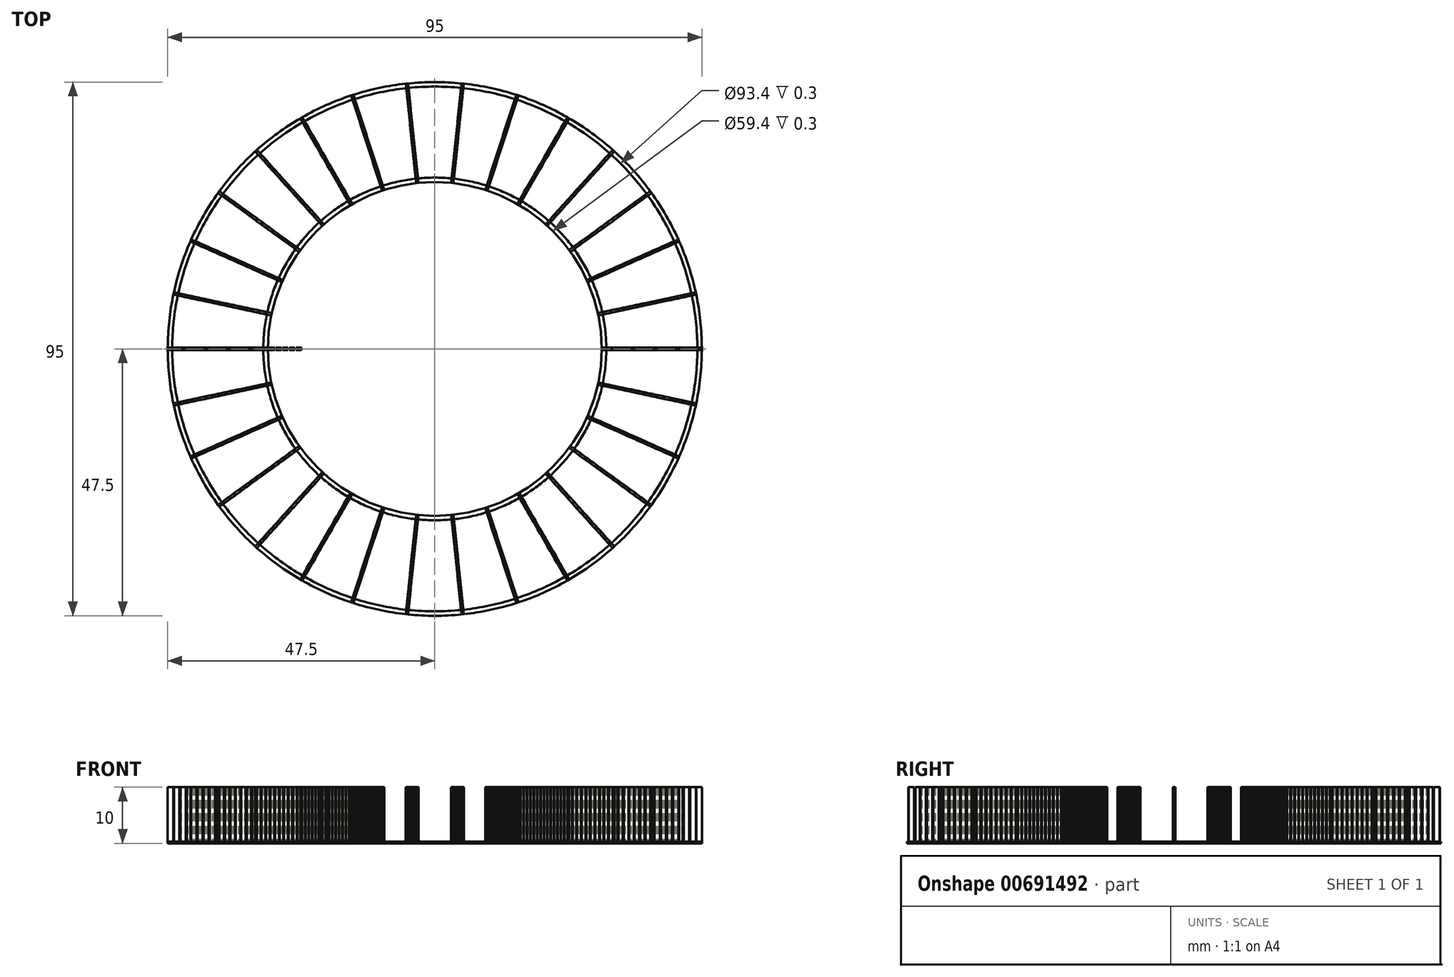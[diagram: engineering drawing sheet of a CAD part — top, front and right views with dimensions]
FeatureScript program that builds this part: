
annotation { "Feature Type Name" : "Feature", "Feature Type Description" : "" }
export const myFeature = defineFeature(function(context is Context, id is Id, definition is map)
    precondition{}
    {
        {
            var Q0;
            Q0=qCreatedBy(makeId("Top.planeOp"),FACE);
            var sketch = newSketch(context, id + "F0", { "sketchPlane" : qUnion([Q0])});
            skCircle(sketch, "E0", {"center": v(0, 0) * mm, "radius": 47.5 * mm, "construction": true});
            skCircle(sketch, "E1", {"center": v(0, 0) * mm, "radius": 30 * mm, "construction": true});
            skLineSegment(sketch, "E2", {"start": v(-30, 0) * mm, "end": v(-47.5, 0) * mm, "construction": true});
            skLineSegment(sketch, "E3.bottom", {"start": v(-30, 0.2) * mm, "end": v(-47.5, 0.2) * mm});
            skLineSegment(sketch, "E3.top", {"start": v(-30, -0.21) * mm, "end": v(-47.5, -0.21) * mm});
            skLineSegment(sketch, "E3.left", {"start": v(-30, 0.2) * mm, "end": v(-30, -0.2) * mm});
            skLineSegment(sketch, "E3.right", {"start": v(-47.5, 0.21) * mm, "end": v(-47.5, -0.21) * mm});
            skSolve(sketch);
        }
        {
            var Q0;
            Q0=makeQuery(id+"F0.imprint","IMPRINT",FACE,{"disambiguationData":[TD([[makeQuery(id+"F0.imprint","IMPRINT",EDGE,{"derivedFrom":sQuery(id+"F0.wireOp",EDGE,"E3.bottom")}),1.0]])]});
            extrude(context, id + "F1", {"entities" : qUnion([Q0]), "depth" : 0.3 * mm, "offsetDistance" : 25 * mm});
        }
        {
            var Q0;
            Q0=qCreatedBy(makeId("Top.planeOp"),FACE);
            var sketch = newSketch(context, id + "F2", { "sketchPlane" : qUnion([Q0])});
            skCircle(sketch, "E4", {"center": v(0, 0) * mm, "radius": 47.5 * mm, "construction": true});
            skCircle(sketch, "E5", {"center": v(0, 0) * mm, "radius": 35 * mm, "construction": true});
            skLineSegment(sketch, "E6", {"start": v(-35, 0) * mm, "end": v(-47.5, 0) * mm, "construction": true});
            skLineSegment(sketch, "E7.bottom", {"start": v(-47.5, 0.2) * mm, "end": v(-46.5, 0.2) * mm});
            skLineSegment(sketch, "E7.top", {"start": v(-47.5, -0.21) * mm, "end": v(-46.5, -0.21) * mm});
            skLineSegment(sketch, "E7.left", {"start": v(-47.5, 0.21) * mm, "end": v(-47.5, -0.21) * mm});
            skLineSegment(sketch, "E7.right", {"start": v(-46.5, 0.21) * mm, "end": v(-46.5, -0.21) * mm});
            skLineSegment(sketch, "E8.1.0.0", {"start": v(-46.3, 0.2) * mm, "end": v(-45.3, 0.2) * mm});
            skLineSegment(sketch, "E8.1.0.1", {"start": v(-45.3, 0.21) * mm, "end": v(-45.3, -0.21) * mm});
            skLineSegment(sketch, "E8.1.0.2", {"start": v(-46.3, -0.21) * mm, "end": v(-45.3, -0.21) * mm});
            skLineSegment(sketch, "E8.1.0.3", {"start": v(-46.3, 0.21) * mm, "end": v(-46.3, -0.21) * mm});
            skLineSegment(sketch, "E8.2.0.0", {"start": v(-45.1, 0.2) * mm, "end": v(-44.1, 0.2) * mm});
            skLineSegment(sketch, "E8.2.0.1", {"start": v(-44.1, 0.21) * mm, "end": v(-44.1, -0.21) * mm});
            skLineSegment(sketch, "E8.2.0.2", {"start": v(-45.1, -0.21) * mm, "end": v(-44.1, -0.21) * mm});
            skLineSegment(sketch, "E8.2.0.3", {"start": v(-45.1, 0.21) * mm, "end": v(-45.1, -0.21) * mm});
            skLineSegment(sketch, "E8.3.0.0", {"start": v(-43.9, 0.2) * mm, "end": v(-42.9, 0.2) * mm});
            skLineSegment(sketch, "E8.3.0.1", {"start": v(-42.9, 0.21) * mm, "end": v(-42.9, -0.21) * mm});
            skLineSegment(sketch, "E8.3.0.2", {"start": v(-43.9, -0.21) * mm, "end": v(-42.9, -0.21) * mm});
            skLineSegment(sketch, "E8.3.0.3", {"start": v(-43.9, 0.21) * mm, "end": v(-43.9, -0.21) * mm});
            skLineSegment(sketch, "E8.4.0.0", {"start": v(-42.7, 0.2) * mm, "end": v(-41.7, 0.2) * mm});
            skLineSegment(sketch, "E8.4.0.1", {"start": v(-41.7, 0.21) * mm, "end": v(-41.7, -0.21) * mm});
            skLineSegment(sketch, "E8.4.0.2", {"start": v(-42.7, -0.21) * mm, "end": v(-41.7, -0.21) * mm});
            skLineSegment(sketch, "E8.4.0.3", {"start": v(-42.7, 0.21) * mm, "end": v(-42.7, -0.21) * mm});
            skLineSegment(sketch, "E8.5.0.0", {"start": v(-41.5, 0.2) * mm, "end": v(-40.5, 0.2) * mm});
            skLineSegment(sketch, "E8.5.0.1", {"start": v(-40.5, 0.21) * mm, "end": v(-40.5, -0.21) * mm});
            skLineSegment(sketch, "E8.5.0.2", {"start": v(-41.5, -0.21) * mm, "end": v(-40.5, -0.21) * mm});
            skLineSegment(sketch, "E8.5.0.3", {"start": v(-41.5, 0.21) * mm, "end": v(-41.5, -0.21) * mm});
            skLineSegment(sketch, "E8.6.0.0", {"start": v(-40.3, 0.2) * mm, "end": v(-39.3, 0.2) * mm});
            skLineSegment(sketch, "E8.6.0.1", {"start": v(-39.3, 0.21) * mm, "end": v(-39.3, -0.21) * mm});
            skLineSegment(sketch, "E8.6.0.2", {"start": v(-40.3, -0.21) * mm, "end": v(-39.3, -0.21) * mm});
            skLineSegment(sketch, "E8.6.0.3", {"start": v(-40.3, 0.21) * mm, "end": v(-40.3, -0.21) * mm});
            skLineSegment(sketch, "E8.7.0.0", {"start": v(-39.1, 0.2) * mm, "end": v(-38.1, 0.2) * mm});
            skLineSegment(sketch, "E8.7.0.1", {"start": v(-38.1, 0.21) * mm, "end": v(-38.1, -0.21) * mm});
            skLineSegment(sketch, "E8.7.0.2", {"start": v(-39.1, -0.21) * mm, "end": v(-38.1, -0.21) * mm});
            skLineSegment(sketch, "E8.7.0.3", {"start": v(-39.1, 0.21) * mm, "end": v(-39.1, -0.21) * mm});
            skLineSegment(sketch, "E8.8.0.0", {"start": v(-37.9, 0.2) * mm, "end": v(-36.9, 0.2) * mm});
            skLineSegment(sketch, "E8.8.0.1", {"start": v(-36.9, 0.21) * mm, "end": v(-36.9, -0.21) * mm});
            skLineSegment(sketch, "E8.8.0.2", {"start": v(-37.9, -0.21) * mm, "end": v(-36.9, -0.21) * mm});
            skLineSegment(sketch, "E8.8.0.3", {"start": v(-37.9, 0.21) * mm, "end": v(-37.9, -0.21) * mm});
            skLineSegment(sketch, "E8.9.0.0", {"start": v(-36.7, 0.2) * mm, "end": v(-35.7, 0.2) * mm});
            skLineSegment(sketch, "E8.9.0.1", {"start": v(-35.7, 0.21) * mm, "end": v(-35.7, -0.21) * mm});
            skLineSegment(sketch, "E8.9.0.2", {"start": v(-36.7, -0.21) * mm, "end": v(-35.7, -0.21) * mm});
            skLineSegment(sketch, "E8.9.0.3", {"start": v(-36.7, 0.21) * mm, "end": v(-36.7, -0.21) * mm});
            skLineSegment(sketch, "E8.10.0.0", {"start": v(-35.5, 0.2) * mm, "end": v(-34.5, 0.2) * mm});
            skLineSegment(sketch, "E8.10.0.1", {"start": v(-34.5, 0.21) * mm, "end": v(-34.5, -0.21) * mm});
            skLineSegment(sketch, "E8.10.0.2", {"start": v(-35.5, -0.21) * mm, "end": v(-34.5, -0.21) * mm});
            skLineSegment(sketch, "E8.10.0.3", {"start": v(-35.5, 0.21) * mm, "end": v(-35.5, -0.21) * mm});
            skLineSegment(sketch, "E8.11.0.0", {"start": v(-34.3, 0.2) * mm, "end": v(-33.3, 0.2) * mm});
            skLineSegment(sketch, "E8.11.0.1", {"start": v(-33.3, 0.21) * mm, "end": v(-33.3, -0.21) * mm});
            skLineSegment(sketch, "E8.11.0.2", {"start": v(-34.3, -0.21) * mm, "end": v(-33.3, -0.21) * mm});
            skLineSegment(sketch, "E8.11.0.3", {"start": v(-34.3, 0.21) * mm, "end": v(-34.3, -0.21) * mm});
            skLineSegment(sketch, "E8.12.0.0", {"start": v(-33.1, 0.2) * mm, "end": v(-32.1, 0.2) * mm});
            skLineSegment(sketch, "E8.12.0.1", {"start": v(-32.1, 0.21) * mm, "end": v(-32.1, -0.21) * mm});
            skLineSegment(sketch, "E8.12.0.2", {"start": v(-33.1, -0.21) * mm, "end": v(-32.1, -0.21) * mm});
            skLineSegment(sketch, "E8.12.0.3", {"start": v(-33.1, 0.21) * mm, "end": v(-33.1, -0.21) * mm});
            skLineSegment(sketch, "E8.13.0.0", {"start": v(-31.9, 0.2) * mm, "end": v(-30.9, 0.2) * mm});
            skLineSegment(sketch, "E8.13.0.1", {"start": v(-30.9, 0.21) * mm, "end": v(-30.9, -0.21) * mm});
            skLineSegment(sketch, "E8.13.0.2", {"start": v(-31.9, -0.21) * mm, "end": v(-30.9, -0.21) * mm});
            skLineSegment(sketch, "E8.13.0.3", {"start": v(-31.9, 0.21) * mm, "end": v(-31.9, -0.21) * mm});
            skLineSegment(sketch, "E8.14.0.0", {"start": v(-30.7, 0.2) * mm, "end": v(-29.7, 0.2) * mm});
            skLineSegment(sketch, "E8.14.0.1", {"start": v(-29.7, 0.21) * mm, "end": v(-29.7, -0.21) * mm});
            skLineSegment(sketch, "E8.14.0.2", {"start": v(-30.7, -0.21) * mm, "end": v(-29.7, -0.21) * mm});
            skLineSegment(sketch, "E8.14.0.3", {"start": v(-30.7, 0.21) * mm, "end": v(-30.7, -0.21) * mm});
            skLineSegment(sketch, "E8.15.0.0", {"start": v(-29.5, 0.2) * mm, "end": v(-28.5, 0.2) * mm});
            skLineSegment(sketch, "E8.15.0.1", {"start": v(-28.5, 0.21) * mm, "end": v(-28.5, -0.21) * mm});
            skLineSegment(sketch, "E8.15.0.2", {"start": v(-29.5, -0.21) * mm, "end": v(-28.5, -0.21) * mm});
            skLineSegment(sketch, "E8.15.0.3", {"start": v(-29.5, 0.21) * mm, "end": v(-29.5, -0.21) * mm});
            skLineSegment(sketch, "E8.direction1", {"start": v(-47.5, 0.2) * mm, "end": v(-46.3, 0.2) * mm, "construction": true});
            skLineSegment(sketch, "E9.0.16.0", {"start": v(-28.3, 0.2) * mm, "end": v(-27.3, 0.2) * mm});
            skLineSegment(sketch, "E9.3.16.0", {"start": v(-27.3, 0.21) * mm, "end": v(-27.3, -0.21) * mm});
            skLineSegment(sketch, "E9.6.16.0", {"start": v(-28.3, -0.21) * mm, "end": v(-27.3, -0.21) * mm});
            skLineSegment(sketch, "E9.9.16.0", {"start": v(-28.3, 0.21) * mm, "end": v(-28.3, -0.21) * mm});
            skLineSegment(sketch, "E9.0.17.0", {"start": v(-27.1, 0.2) * mm, "end": v(-26.1, 0.2) * mm});
            skLineSegment(sketch, "E9.3.17.0", {"start": v(-26.1, 0.21) * mm, "end": v(-26.1, -0.21) * mm});
            skLineSegment(sketch, "E9.6.17.0", {"start": v(-27.1, -0.21) * mm, "end": v(-26.1, -0.21) * mm});
            skLineSegment(sketch, "E9.9.17.0", {"start": v(-27.1, 0.21) * mm, "end": v(-27.1, -0.21) * mm});
            skLineSegment(sketch, "E9.0.18.0", {"start": v(-25.9, 0.2) * mm, "end": v(-24.9, 0.2) * mm});
            skLineSegment(sketch, "E9.3.18.0", {"start": v(-24.9, 0.21) * mm, "end": v(-24.9, -0.21) * mm});
            skLineSegment(sketch, "E9.6.18.0", {"start": v(-25.9, -0.21) * mm, "end": v(-24.9, -0.21) * mm});
            skLineSegment(sketch, "E9.9.18.0", {"start": v(-25.9, 0.21) * mm, "end": v(-25.9, -0.21) * mm});
            skLineSegment(sketch, "E10.0.19.0", {"start": v(-24.7, 0.2) * mm, "end": v(-23.7, 0.2) * mm});
            skLineSegment(sketch, "E10.3.19.0", {"start": v(-23.7, 0.21) * mm, "end": v(-23.7, -0.21) * mm});
            skLineSegment(sketch, "E10.6.19.0", {"start": v(-24.7, -0.21) * mm, "end": v(-23.7, -0.21) * mm});
            skLineSegment(sketch, "E10.9.19.0", {"start": v(-24.7, 0.21) * mm, "end": v(-24.7, -0.21) * mm});
            skSolve(sketch);
        }
        {
            var Q0;
            Q0 = qSketchRegion(id + "F2", true);
            extrude(context, id + "F3", {"entities" : qUnion([Q0]), "operationType" : NewBodyOperationType.ADD, "depth" : 10 * mm, "offsetDistance" : 25 * mm});
        }
        {
            var Q0;
            Q0=qCreatedBy(makeId("Front.planeOp"),FACE);
            var sketch = newSketch(context, id + "F4", { "sketchPlane" : qUnion([Q0])});
            skLineSegment(sketch, "E11", {"start": v(0, 0) * mm, "end": v(0, 21.5) * mm, "construction": true});
            skSolve(sketch);
        }
        {
            var Q0;
            Q0=makeQuery(id+"F1.opExtrude","SWEPT_BODY",BODY,{"disambiguationData":[OSD([sQuery(id+"F0.wireOp",EDGE,"E3.bottom"),sQuery(id+"F0.wireOp",EDGE,"E3.top"),sQuery(id+"F0.wireOp",EDGE,"E3.left"),sQuery(id+"F0.wireOp",EDGE,"E3.right")])]});
            var Q1;
            Q1=sQuery(id+"F4.wireOp",EDGE,"E11");
            circularPattern(context, id + "F5", {"entities" : qUnion([Q0]), "axis" : qUnion([Q1]), "angle" : 360 * degree, "instanceCount" : 30, "equalSpace" : true});
        }
        {
            var Q0;
            Q0=makeQuery(id+"F3.boolean.opBoolean","MERGE",FACE,{"derivedFrom":[makeQuery(id+"F1.opExtrude","CAP_FACE",FACE,{"disambiguationData":[OSD([sQuery(id+"F0.wireOp",EDGE,"E3.bottom"),sQuery(id+"F0.wireOp",EDGE,"E3.top"),sQuery(id+"F0.wireOp",EDGE,"E3.left"),sQuery(id+"F0.wireOp",EDGE,"E3.right")])],"isStart":true}),makeQuery(id+"F3.opExtrude","CAP_FACE",FACE,{"disambiguationData":[OSD([sQuery(id+"F2.wireOp",EDGE,"E8.15.0.0"),sQuery(id+"F2.wireOp",EDGE,"E8.15.0.1"),sQuery(id+"F2.wireOp",EDGE,"E8.15.0.2"),sQuery(id+"F2.wireOp",EDGE,"E8.15.0.3")])],"isStart":true})]});
            var sketch = newSketch(context, id + "F6", { "sketchPlane" : qUnion([Q0])});
            skPoint(sketch, "E12.0", {"position": v(0, 0) * mm});
            skCircle(sketch, "E13", {"center": v(0, 0) * mm, "radius": 47.5 * mm});
            skCircle(sketch, "E14", {"center": v(0, 0) * mm, "radius": 46.7 * mm});
            skCircle(sketch, "E15.0", {"center": v(0, 0) * mm, "radius": 47.5 * mm, "construction": true});
            skSolve(sketch);
        }
        {
            var Q0;
            Q0 = qSketchRegion(id + "F6", true);
            extrude(context, id + "F7", {"entities" : qUnion([Q0]), "oppositeDirection" : true, "depth" : 0.3 * mm, "offsetDistance" : 25 * mm});
        }
        {
            var Q0;
            Q0=makeQuery(id+"F3.boolean.opBoolean","MERGE",FACE,{"derivedFrom":[makeQuery(id+"F1.opExtrude","CAP_FACE",FACE,{"disambiguationData":[OSD([sQuery(id+"F0.wireOp",EDGE,"E3.bottom"),sQuery(id+"F0.wireOp",EDGE,"E3.top"),sQuery(id+"F0.wireOp",EDGE,"E3.left"),sQuery(id+"F0.wireOp",EDGE,"E3.right")])],"isStart":true}),makeQuery(id+"F3.opExtrude","CAP_FACE",FACE,{"disambiguationData":[OSD([sQuery(id+"F2.wireOp",EDGE,"E8.15.0.0"),sQuery(id+"F2.wireOp",EDGE,"E8.15.0.1"),sQuery(id+"F2.wireOp",EDGE,"E8.15.0.2"),sQuery(id+"F2.wireOp",EDGE,"E8.15.0.3")])],"isStart":true})]});
            var sketch = newSketch(context, id + "F8", { "sketchPlane" : qUnion([Q0])});
            skPoint(sketch, "E16.0", {"position": v(0, 0) * mm});
            skCircle(sketch, "E17", {"center": v(0, 0) * mm, "radius": 29.7 * mm});
            skCircle(sketch, "E18", {"center": v(0, 0) * mm, "radius": 30.5 * mm});
            skSolve(sketch);
        }
        {
            var Q0;
            Q0 = qSketchRegion(id + "F8", true);
            extrude(context, id + "F9", {"entities" : qUnion([Q0]), "oppositeDirection" : true, "depth" : 0.3 * mm, "offsetDistance" : 25 * mm});
        }
    });
